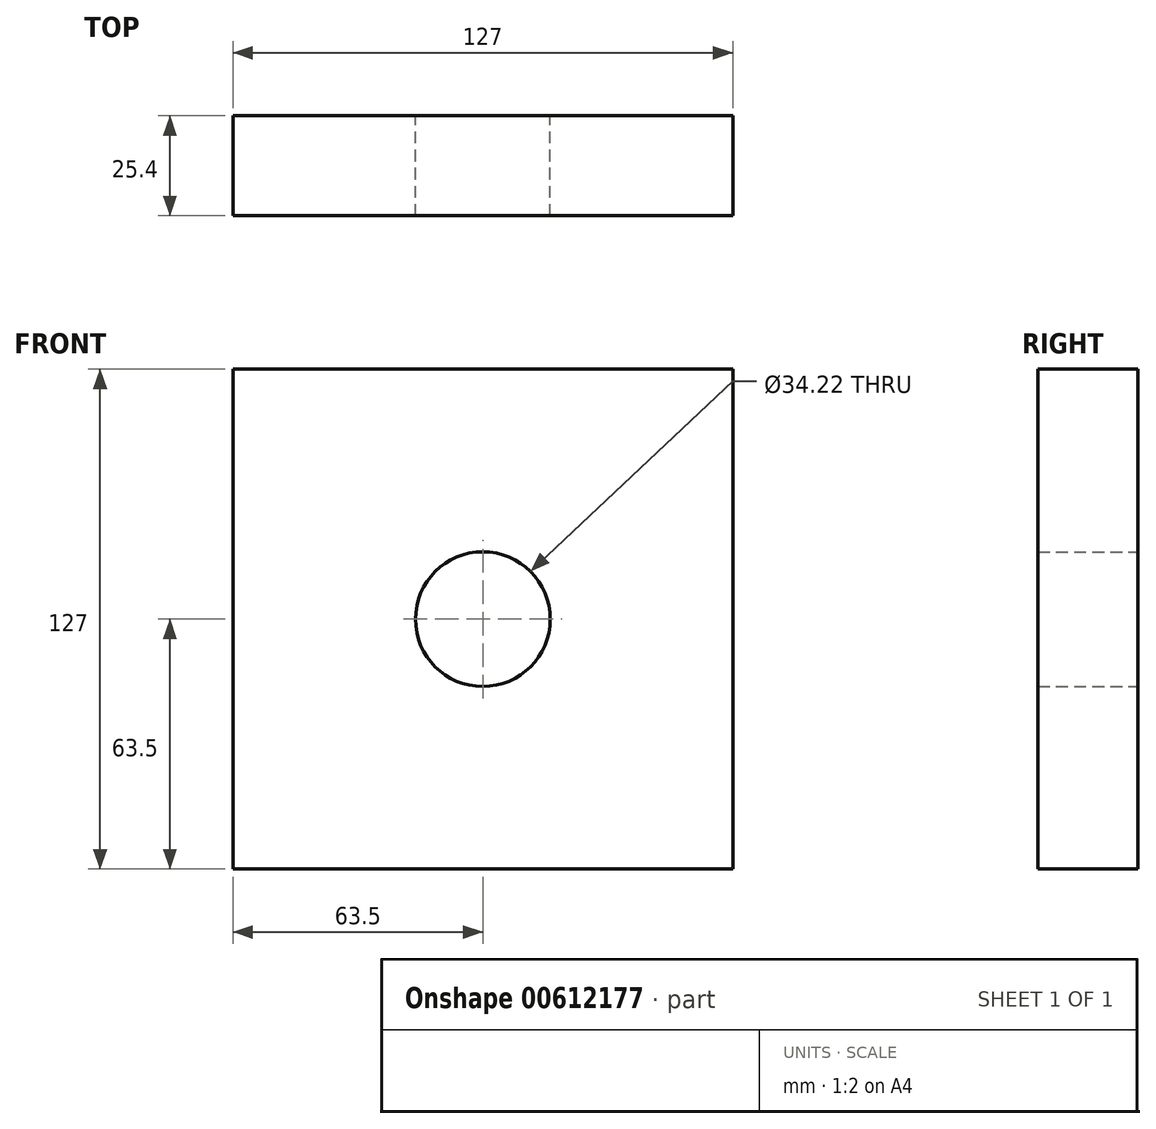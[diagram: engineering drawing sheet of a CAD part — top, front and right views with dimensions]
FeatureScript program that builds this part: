
annotation { "Feature Type Name" : "Feature", "Feature Type Description" : "" }
export const myFeature = defineFeature(function(context is Context, id is Id, definition is map)
    precondition{}
    {
        {
            var Q0;
            Q0=qCreatedBy(makeId("Front.planeOp"),FACE);
            var sketch = newSketch(context, id + "F0", { "sketchPlane" : qUnion([Q0])});
            skLineSegment(sketch, "E0.bottom", {"start": v(0, 0) * mm, "end": v(-127, 0) * mm});
            skLineSegment(sketch, "E0.top", {"start": v(0, 127) * mm, "end": v(-127, 127) * mm});
            skLineSegment(sketch, "E0.left", {"start": v(0, 0) * mm, "end": v(0, 127) * mm});
            skLineSegment(sketch, "E0.right", {"start": v(-127, 0) * mm, "end": v(-127, 127) * mm});
            skLineSegment(sketch, "E1", {"start": v(-127, 127) * mm, "end": v(0, 0) * mm, "construction": true});
            skLineSegment(sketch, "E2", {"start": v(0, 127) * mm, "end": v(-127, 0) * mm, "construction": true});
            skCircle(sketch, "E3", {"center": v(-63.5, 63.5) * mm, "radius": 17.11 * mm});
            skSolve(sketch);
        }
        {
            var Q0;
            Q0 = qSketchRegion(id + "F0", true);
            extrude(context, id + "F1", {"entities" : qUnion([Q0]), "depth" : 25.4 * mm, "offsetDistance" : 25.4 * mm});
        }
    });
